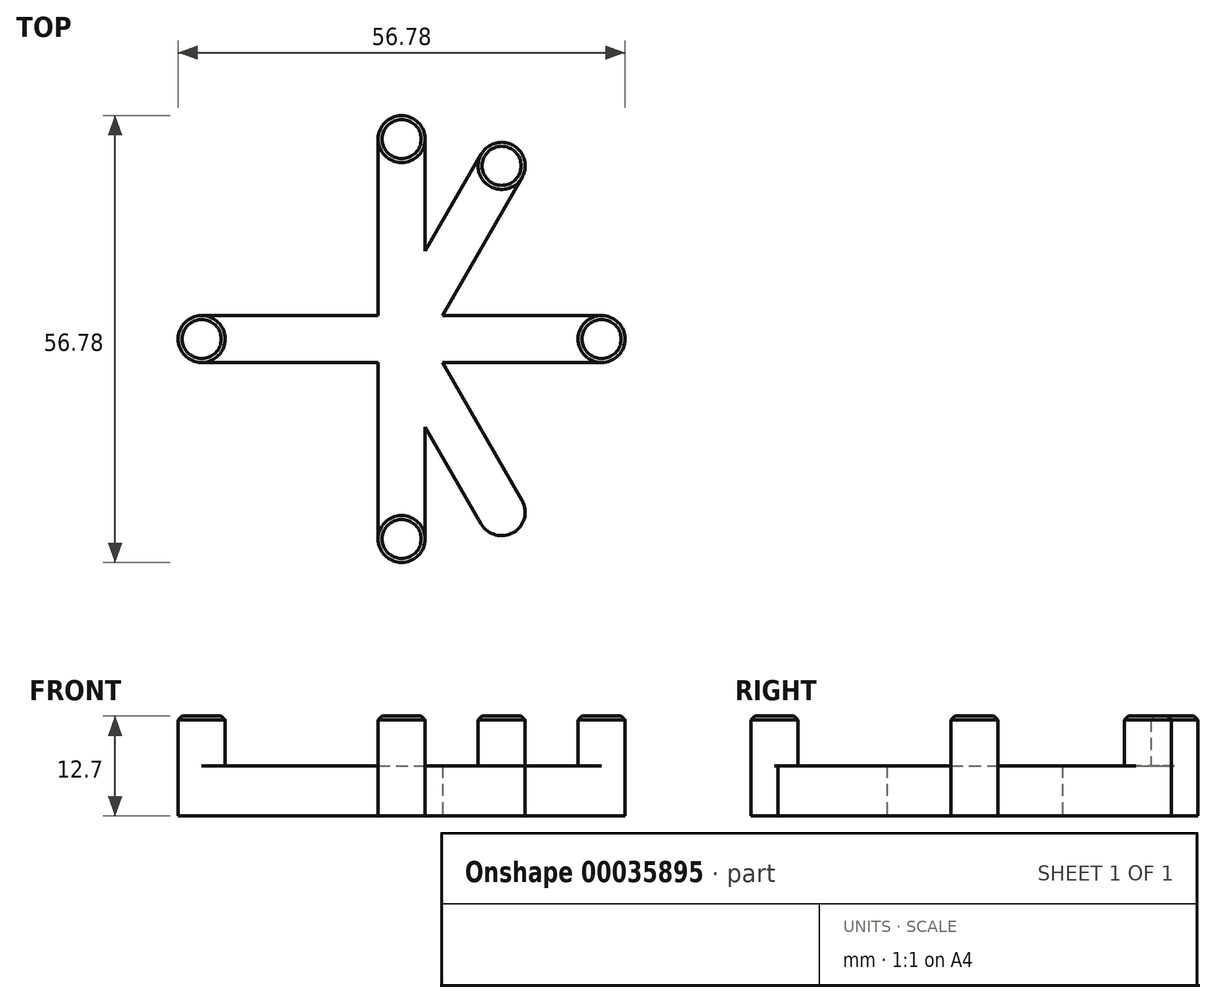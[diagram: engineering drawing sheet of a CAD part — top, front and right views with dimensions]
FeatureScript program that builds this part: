
annotation { "Feature Type Name" : "Feature", "Feature Type Description" : "" }
export const myFeature = defineFeature(function(context is Context, id is Id, definition is map)
    precondition{}
    {
        {
            var Q0;
            Q0=qCreatedBy(makeId("Top.planeOp"),FACE);
            var sketch = newSketch(context, id + "F0", { "sketchPlane" : qUnion([Q0])});
            skLineSegment(sketch, "E0.rect.bottom", {"start": v(3, -25.4) * mm, "end": v(-3, -25.4) * mm, "construction": true});
            skLineSegment(sketch, "E0.rect.top", {"start": v(3, 25.4) * mm, "end": v(-3, 25.4) * mm, "construction": true});
            skLineSegment(sketch, "E0.rect.left", {"start": v(3, -25.4) * mm, "end": v(3, 25.4) * mm});
            skLineSegment(sketch, "E0.rect.right", {"start": v(-3, -25.4) * mm, "end": v(-3, 25.4) * mm});
            skPoint(sketch, "E0.rect.middle", {"position": v(0, 0) * mm});
            skLineSegment(sketch, "E1.rect.bottom", {"start": v(25.4, 3) * mm, "end": v(-25.4, 3) * mm});
            skLineSegment(sketch, "E1.rect.top", {"start": v(25.4, -3) * mm, "end": v(-25.4, -3) * mm});
            skLineSegment(sketch, "E1.rect.left", {"start": v(25.4, 3) * mm, "end": v(25.4, -3) * mm, "construction": true});
            skLineSegment(sketch, "E1.rect.right", {"start": v(-25.4, 3) * mm, "end": v(-25.4, -3) * mm, "construction": true});
            skCircle(sketch, "E2", {"center": v(-25.4, 0) * mm, "radius": 3 * mm});
            skCircle(sketch, "E3", {"center": v(0, 25.4) * mm, "radius": 3 * mm});
            skCircle(sketch, "E4", {"center": v(25.4, 0) * mm, "radius": 3 * mm});
            skCircle(sketch, "E5", {"center": v(0, -25.4) * mm, "radius": 3 * mm});
            skSolve(sketch);
        }
        {
            var Q0;
            {var subQ0=sQuery(id+"F0.wireOp",EDGE,"E0.rect.top");Q0=makeQuery(id+"F0.imprint","IMPRINT",FACE,{"disambiguationData":[TD([[makeQuery(id+"F0.imprint","IMPRINT",EDGE,{"derivedFrom":subQ0}),1.0]])]});}
            var Q1;
            {var subQ0=sQuery(id+"F0.wireOp",EDGE,"E1.rect.top");var subQ3=sQuery(id+"F0.wireOp",EDGE,"E0.rect.left");var subQ4=makeQuery(id+"F0.imprint","INTERSECT",VERTEX,{"derivedFrom":[subQ3,subQ0]});Q1=makeQuery(id+"F0.imprint","IMPRINT",FACE,{"disambiguationData":[TD([[makeQuery(id+"F0.imprint","IMPRINT",EDGE,{"disambiguationData":[TD([[subQ4,-1.0]])],"derivedFrom":subQ3}),1.0]])]});}
            var Q2;
            {var subQ3=sQuery(id+"F0.wireOp",EDGE,"E1.rect.right");Q2=makeQuery(id+"F0.imprint","IMPRINT",FACE,{"disambiguationData":[TD([[makeQuery(id+"F0.imprint","IMPRINT",EDGE,{"derivedFrom":subQ3}),1.0]])]});}
            var Q3;
            {var subQ0=sQuery(id+"F0.wireOp",EDGE,"E0.rect.bottom");Q3=makeQuery(id+"F0.imprint","IMPRINT",FACE,{"disambiguationData":[TD([[makeQuery(id+"F0.imprint","IMPRINT",EDGE,{"derivedFrom":subQ0}),-1.0]])]});}
            var Q4;
            {var subQ5=sQuery(id+"F0.wireOp",EDGE,"E1.rect.left");Q4=makeQuery(id+"F0.imprint","IMPRINT",FACE,{"disambiguationData":[TD([[makeQuery(id+"F0.imprint","IMPRINT",EDGE,{"derivedFrom":subQ5}),-1.0]])]});}
            var Q5;
            {var subQ3=sQuery(id+"F0.wireOp",EDGE,"E0.rect.left");var subQ5=sQuery(id+"F0.wireOp",EDGE,"E1.rect.bottom");var subQ7=makeQuery(id+"F0.imprint","INTERSECT",VERTEX,{"derivedFrom":[subQ3,subQ5]});Q5=makeQuery(id+"F0.imprint","IMPRINT",FACE,{"disambiguationData":[TD([[makeQuery(id+"F0.imprint","IMPRINT",EDGE,{"disambiguationData":[TD([[subQ7,-1.0]])],"derivedFrom":subQ3}),1.0]])]});}
            var Q6;
            {var subQ0=sQuery(id+"F0.wireOp",EDGE,"E1.rect.top");var subQ3=sQuery(id+"F0.wireOp",EDGE,"E0.rect.right");var subQ4=makeQuery(id+"F0.imprint","INTERSECT",VERTEX,{"derivedFrom":[subQ3,subQ0]});Q6=makeQuery(id+"F0.imprint","IMPRINT",FACE,{"disambiguationData":[TD([[makeQuery(id+"F0.imprint","IMPRINT",EDGE,{"disambiguationData":[TD([[subQ4,-1.0]])],"derivedFrom":subQ3}),1.0]])]});}
            var Q7;
            {var subQ0=sQuery(id+"F0.wireOp",EDGE,"E1.rect.top");var subQ3=sQuery(id+"F0.wireOp",EDGE,"E0.rect.left");var subQ4=makeQuery(id+"F0.imprint","INTERSECT",VERTEX,{"derivedFrom":[subQ3,subQ0]});Q7=makeQuery(id+"F0.imprint","IMPRINT",FACE,{"disambiguationData":[TD([[makeQuery(id+"F0.imprint","IMPRINT",EDGE,{"disambiguationData":[TD([[subQ4,-1.0]])],"derivedFrom":subQ3}),-1.0]])]});}
            var Q8;
            {var subQ0=sQuery(id+"F0.wireOp",EDGE,"E5");var subQ3=sQuery(id+"F0.wireOp",EDGE,"E0.rect.left");var subQ4=makeQuery(id+"F0.imprint","INTERSECT",VERTEX,{"derivedFrom":[subQ3,subQ0]});Q8=makeQuery(id+"F0.imprint","IMPRINT",FACE,{"disambiguationData":[TD([[makeQuery(id+"F0.imprint","IMPRINT",EDGE,{"disambiguationData":[TD([[subQ4,-1.0]])],"derivedFrom":subQ3}),1.0]])]});}
            var Q9;
            {var subQ0=sQuery(id+"F0.wireOp",EDGE,"E4");var subQ2=makeQuery(id+"F0.imprint","INTERSECT",VERTEX,{"derivedFrom":[sQuery(id+"F0.wireOp",EDGE,"E1.rect.bottom"),subQ0]});Q9=makeQuery(id+"F0.imprint","IMPRINT",FACE,{"disambiguationData":[TD([[makeQuery(id+"F0.imprint","IMPRINT",EDGE,{"disambiguationData":[TD([[subQ2,-1.0]])],"derivedFrom":subQ0}),1.0]])]});}
            var Q10;
            {var subQ0=sQuery(id+"F0.wireOp",EDGE,"E2");var subQ2=makeQuery(id+"F0.imprint","INTERSECT",VERTEX,{"derivedFrom":[sQuery(id+"F0.wireOp",EDGE,"E1.rect.bottom"),subQ0]});Q10=makeQuery(id+"F0.imprint","IMPRINT",FACE,{"disambiguationData":[TD([[makeQuery(id+"F0.imprint","IMPRINT",EDGE,{"disambiguationData":[TD([[subQ2,-1.0]])],"derivedFrom":subQ0}),1.0]])]});}
            var Q11;
            {var subQ0=sQuery(id+"F0.wireOp",EDGE,"E5");var subQ2=makeQuery(id+"F0.imprint","INTERSECT",VERTEX,{"derivedFrom":[sQuery(id+"F0.wireOp",EDGE,"E0.rect.left"),subQ0]});Q11=makeQuery(id+"F0.imprint","IMPRINT",FACE,{"disambiguationData":[TD([[makeQuery(id+"F0.imprint","IMPRINT",EDGE,{"disambiguationData":[TD([[subQ2,-1.0]])],"derivedFrom":subQ0}),1.0]])]});}
            var Q12;
            {var subQ0=sQuery(id+"F0.wireOp",EDGE,"E3");var subQ2=makeQuery(id+"F0.imprint","INTERSECT",VERTEX,{"derivedFrom":[sQuery(id+"F0.wireOp",EDGE,"E0.rect.left"),subQ0]});Q12=makeQuery(id+"F0.imprint","IMPRINT",FACE,{"disambiguationData":[TD([[makeQuery(id+"F0.imprint","IMPRINT",EDGE,{"disambiguationData":[TD([[subQ2,-1.0]])],"derivedFrom":subQ0}),1.0]])]});}
            extrude(context, id + "F1", {"entities" : qUnion([Q0, Q1, Q2, Q3, Q4, Q5, Q6, Q7, Q8, Q9, Q10, Q11, Q12]), "depth" : 6.35 * mm});
        }
        {
            var Q0;
            Q0=makeQuery(id+"F0.imprint","IMPRINT",FACE,{"disambiguationData":[TD([[makeQuery(id+"F0.imprint","IMPRINT",EDGE,{"derivedFrom":sQuery(id+"F0.wireOp",EDGE,"E5")}),1.0]])]});
            var Q1;
            Q1=makeQuery(id+"F0.imprint","IMPRINT",FACE,{"disambiguationData":[TD([[makeQuery(id+"F0.imprint","IMPRINT",EDGE,{"derivedFrom":sQuery(id+"F0.wireOp",EDGE,"E2")}),1.0]])]});
            var Q2;
            Q2=makeQuery(id+"F0.imprint","IMPRINT",FACE,{"disambiguationData":[TD([[makeQuery(id+"F0.imprint","IMPRINT",EDGE,{"derivedFrom":sQuery(id+"F0.wireOp",EDGE,"E4")}),1.0]])]});
            var Q3;
            Q3=makeQuery(id+"F0.imprint","IMPRINT",FACE,{"disambiguationData":[TD([[makeQuery(id+"F0.imprint","IMPRINT",EDGE,{"derivedFrom":sQuery(id+"F0.wireOp",EDGE,"E3")}),1.0]])]});
            extrude(context, id + "F2", {"entities" : qUnion([Q0, Q1, Q2, Q3]), "operationType" : NewBodyOperationType.ADD, "depth" : 12.7 * mm});
        }
        {
            var Q0;
            Q0=makeQuery(id+"F2.opExtrude","CAP_EDGE",EDGE,{"disambiguationData":[OSD([sQuery(id+"F0.wireOp",EDGE,"E4")])],"isStart":false});
            var Q1;
            Q1=makeQuery(id+"F2.opExtrude","CAP_EDGE",EDGE,{"disambiguationData":[OSD([sQuery(id+"F0.wireOp",EDGE,"E5")])],"isStart":false});
            var Q2;
            Q2=makeQuery(id+"F2.opExtrude","CAP_EDGE",EDGE,{"disambiguationData":[OSD([sQuery(id+"F0.wireOp",EDGE,"E2")])],"isStart":false});
            var Q3;
            Q3=makeQuery(id+"F2.opExtrude","CAP_EDGE",EDGE,{"disambiguationData":[OSD([sQuery(id+"F0.wireOp",EDGE,"E3")])],"isStart":false});
            chamfer(context, id + "F3", {"entities" : qUnion([Q0, Q1, Q2, Q3]), "width" : 0.5 * mm, "tangentPropagation" : true});
        }
        {
            var Q0;
            Q0=qCreatedBy(makeId("Top.planeOp"),FACE);
            var sketch = newSketch(context, id + "F4", { "sketchPlane" : qUnion([Q0])});
            skCircle(sketch, "E6", {"center": v(0, 0) * mm, "radius": 3 * mm, "construction": true});
            skLineSegment(sketch, "E7.bottom", {"start": v(-25.4, 3) * mm, "end": v(0, 3) * mm});
            skLineSegment(sketch, "E7.top", {"start": v(-25.4, -3) * mm, "end": v(0, -3) * mm});
            skLineSegment(sketch, "E7.left", {"start": v(-25.4, 3) * mm, "end": v(-25.4, -3) * mm, "construction": true});
            skLineSegment(sketch, "E7.right", {"start": v(0, 3) * mm, "end": v(0, -3) * mm});
            skCircle(sketch, "E8", {"center": v(-25.4, 0) * mm, "radius": 3 * mm});
            skLineSegment(sketch, "E9", {"start": v(-2.6, 1.5) * mm, "end": v(10.1, 23.5) * mm});
            skLineSegment(sketch, "E10", {"start": v(2.6, -1.5) * mm, "end": v(15.3, 20.5) * mm});
            skLineSegment(sketch, "E11", {"start": v(10.1, 23.5) * mm, "end": v(15.3, 20.5) * mm, "construction": true});
            skCircle(sketch, "E12", {"center": v(12.7, 22) * mm, "radius": 3 * mm});
            skLineSegment(sketch, "E13", {"start": v(0, 0) * mm, "end": v(24, 0) * mm, "construction": true});
            skLineSegment(sketch, "E14.MirrorCS", {"start": v(2.6, 1.5) * mm, "end": v(15.3, -20.5) * mm});
            skLineSegment(sketch, "E15.MirrorCS", {"start": v(-2.6, -1.5) * mm, "end": v(10.1, -23.5) * mm});
            skCircle(sketch, "E16.MirrorC", {"center": v(12.7, -22) * mm, "radius": 3 * mm});
            skSolve(sketch);
        }
        {
            var Q0;
            Q0 = qSketchRegion(id + "F4", true);
            extrude(context, id + "F5", {"entities" : qUnion([Q0]), "depth" : 6.35 * mm});
        }
        {
            var Q0;
            {var subQ0=sQuery(id+"F4.wireOp",EDGE,"E12");var subQ2=makeQuery(id+"F4.imprint","INTERSECT",VERTEX,{"derivedFrom":[sQuery(id+"F4.wireOp",EDGE,"E9"),subQ0]});Q0=makeQuery(id+"F4.imprint","IMPRINT",FACE,{"disambiguationData":[TD([[makeQuery(id+"F4.imprint","IMPRINT",EDGE,{"disambiguationData":[TD([[subQ2,-1.0]])],"derivedFrom":subQ0}),1.0]])]});}
            var Q1;
            {var subQ0=sQuery(id+"F4.wireOp",EDGE,"E8");var subQ2=makeQuery(id+"F4.imprint","INTERSECT",VERTEX,{"derivedFrom":[sQuery(id+"F4.wireOp",EDGE,"E7.bottom"),subQ0]});Q1=makeQuery(id+"F4.imprint","IMPRINT",FACE,{"disambiguationData":[TD([[makeQuery(id+"F4.imprint","IMPRINT",EDGE,{"disambiguationData":[TD([[subQ2,-1.0]])],"derivedFrom":subQ0}),1.0]])]});}
            var Q2;
            {var subQ0=sQuery(id+"F4.wireOp",EDGE,"E16.MirrorC");var subQ2=makeQuery(id+"F4.imprint","INTERSECT",VERTEX,{"derivedFrom":[sQuery(id+"F4.wireOp",EDGE,"E14.MirrorCS"),subQ0]});Q2=makeQuery(id+"F4.imprint","IMPRINT",FACE,{"disambiguationData":[TD([[makeQuery(id+"F4.imprint","IMPRINT",EDGE,{"disambiguationData":[TD([[subQ2,1.0]])],"derivedFrom":subQ0}),-1.0]])]});}
            extrude(context, id + "F6", {"entities" : qUnion([Q0, Q1, Q2]), "operationType" : NewBodyOperationType.ADD, "depth" : 12.7 * mm});
        }
        {
            var Q0;
            Q0=makeQuery(id+"F6.opExtrude","CAP_EDGE",EDGE,{"disambiguationData":[OSD([sQuery(id+"F4.wireOp",EDGE,"E8")])],"isStart":false});
            var Q1;
            Q1=makeQuery(id+"F6.opExtrude","CAP_EDGE",EDGE,{"disambiguationData":[OSD([sQuery(id+"F4.wireOp",EDGE,"E12")])],"isStart":false});
            var Q2;
            Q2=makeQuery(id+"F6.opExtrude","CAP_EDGE",EDGE,{"disambiguationData":[OSD([sQuery(id+"F4.wireOp",EDGE,"E16.MirrorC")])],"isStart":false});
            chamfer(context, id + "F7", {"entities" : qUnion([Q0, Q1, Q2]), "width" : 0.5 * mm, "tangentPropagation" : true});
        }
    });
